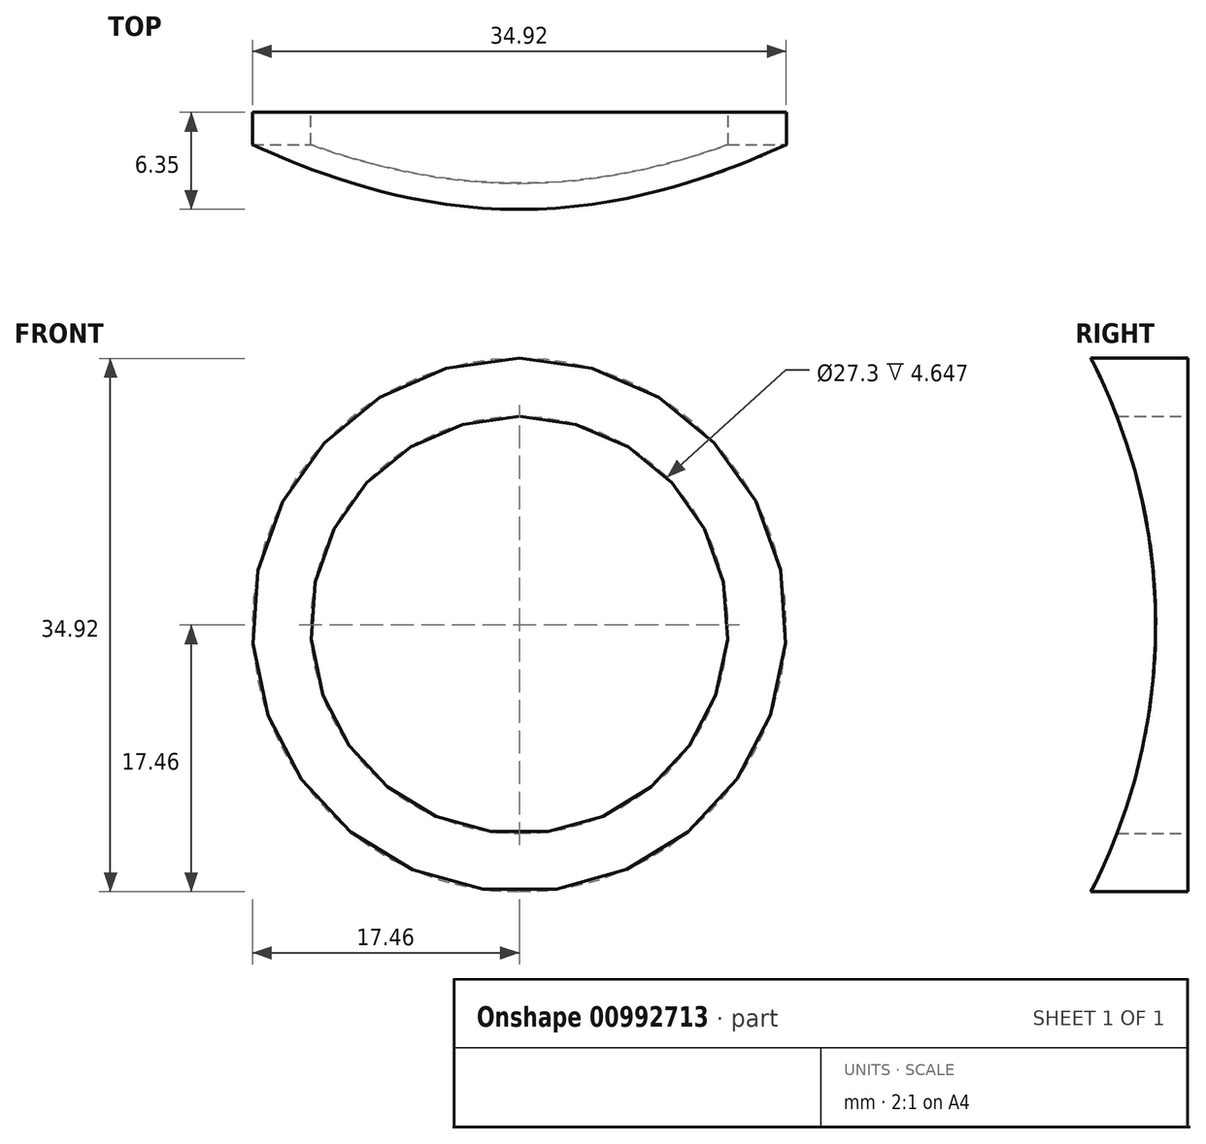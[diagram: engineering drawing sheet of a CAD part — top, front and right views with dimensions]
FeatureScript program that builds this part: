
annotation { "Feature Type Name" : "Feature", "Feature Type Description" : "" }
export const myFeature = defineFeature(function(context is Context, id is Id, definition is map)
    precondition{}
    {
        {
            var Q0;
            Q0=qCreatedBy(makeId("Front.planeOp"),FACE);
            var sketch = newSketch(context, id + "F0", { "sketchPlane" : qUnion([Q0])});
            skCircle(sketch, "E0", {"center": v(0, 0) * mm, "radius": 17.46 * mm});
            skCircle(sketch, "E1", {"center": v(0, 0) * mm, "radius": 13.65 * mm});
            skSolve(sketch);
        }
        {
            var Q0;
            Q0=qSketchRegion(id+"F0",true);
            extrude(context, id + "F1", {"entities" : qUnion([Q0]), "depth" : 6.35 * mm, "offsetDistance" : 25.4 * mm});
        }
        {
            var Q0;
            Q0=qCreatedBy(makeId("Right.planeOp"),FACE);
            var sketch = newSketch(context, id + "F2", { "sketchPlane" : qUnion([Q0])});
            skLineSegment(sketch, "E2.0", {"start": v(-6.35, -17.46) * mm, "end": v(-6.35, 17.46) * mm, "construction": true});
            skArc(sketch, "E3", {"start": v(-6.35, -17.46) * mm, "mid": v(-2.11, 0) * mm, "end": v(-6.35, 17.46) * mm});
            skLineSegment(sketch, "E4", {"start": v(-6.35, 17.46) * mm, "end": v(-6.35, -17.46) * mm});
            skSolve(sketch);
        }
        {
            var Q0;
            Q0=qSketchRegion(id+"F2",true);
            extrude(context, id + "F3", {"entities" : qUnion([Q0]), "operationType" : NewBodyOperationType.REMOVE, "endBound" : BoundingType.THROUGH_ALL, "oppositeDirection" : true, "depth" : 25.4 * mm, "offsetDistance" : 25.4 * mm, "hasSecondDirection" : true, "secondDirectionBound" : SecondDirectionBoundingType.THROUGH_ALL, "secondDirectionOppositeDirection" : false, "secondDirectionDepth" : 25.4 * mm});
        }
    });
